# Revit family: 05302_DSA
name_source: partatom
category: Air Terminals
revit_build: Autodesk Revit MEP 2012 (Build: 20110309_2315(x64)
units: mm (PartAtom-declared; Revit-internal decimal feet)

## types (5) — shared parameters
Cuello Mín-Máx. = 8" hasta 20"
Description = Difusor de Largo Alcance
Función = Inyección
Incrementos de Cuello = de 2"
Manufacturer = INNES
Material = Aluminio
Model = DSA
Nota1 = .
Tipo de Cuello = Redondo
Type Comments = Deflector anti-condensación
URL = https://www.innes.com.mx
Visible_Texto = No

## per-type parameters (varying)
| type | Conect | Posición de Instalación | Tamanio_Requerido | Var_Conect | Var_Tamanio |
| DSA-08" | 3 25/64" | Muro
Muro | 8 | 6 25/32" | 8" |
| DSA-10" | 4 7/8" | Muro
Muro/Techo | 10 | 9 49/64" | 10" |
| DSA-12" | 5 43/64" | Muro
Muro/Techo | 12 | 11 23/64" | 12" |
| DSA-16" | 7 57/64" | Muro
Muro/Techo | 16 | 15 49/64" | 16" |
| DSA-20" | 9 3/32" | Muro
Muro/Techo | 20 | 18 3/16" | 20" |

## geometry (parser evidence)
native form markers: Sweep x3
no freeform markers — native parametric forms only
